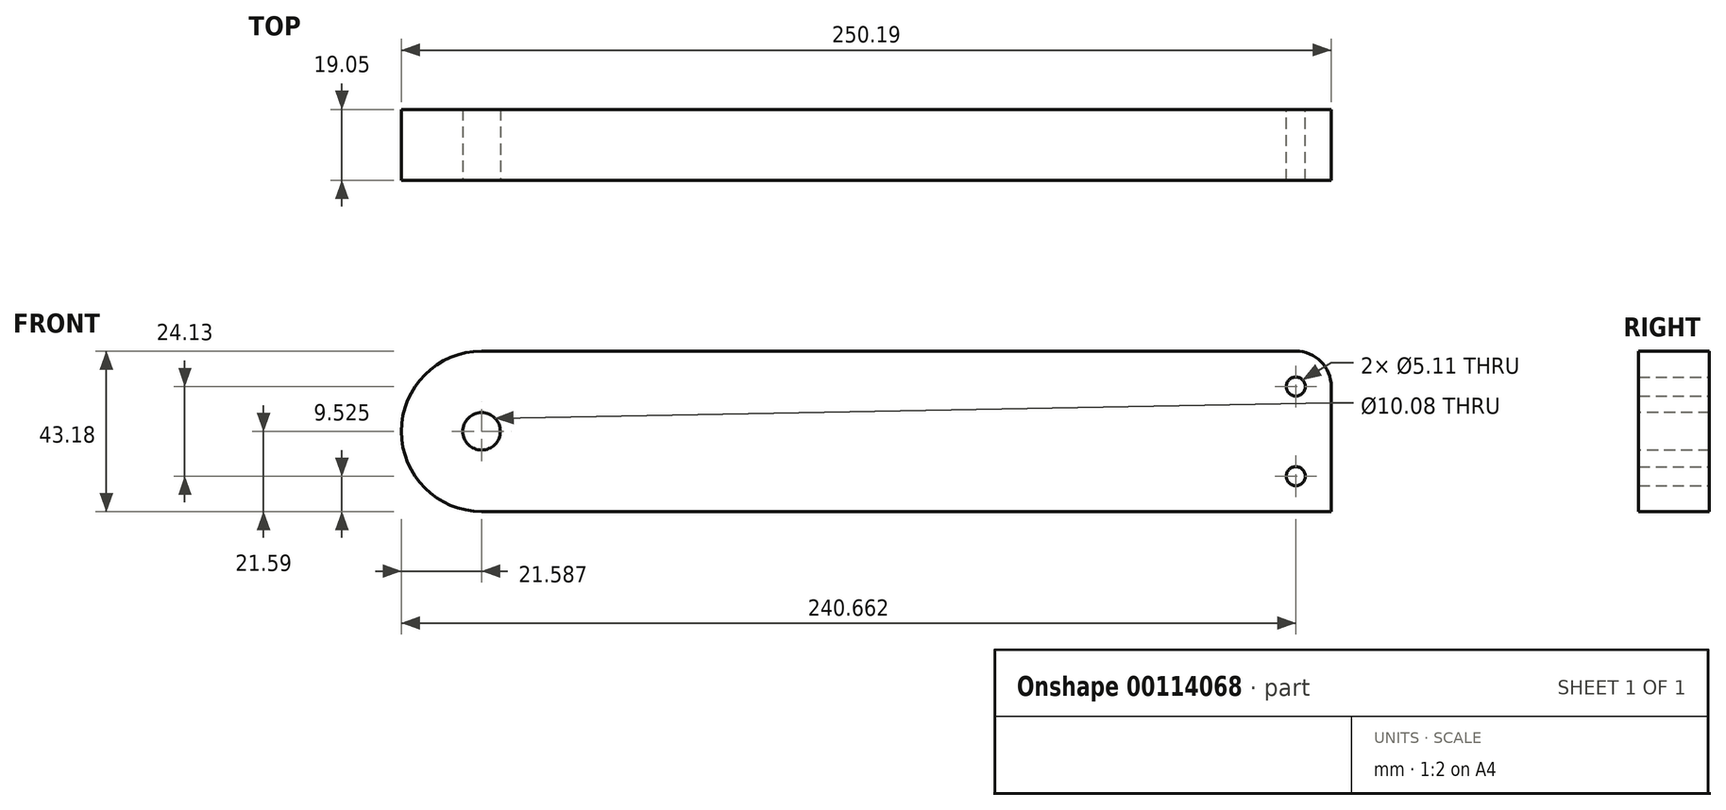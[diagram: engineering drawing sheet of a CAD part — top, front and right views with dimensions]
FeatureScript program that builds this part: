
annotation { "Feature Type Name" : "Feature", "Feature Type Description" : "" }
export const myFeature = defineFeature(function(context is Context, id is Id, definition is map)
    precondition{}
    {
        {
            var Q0;
            Q0=qCreatedBy(makeId("Front.planeOp"),FACE);
            var sketch = newSketch(context, id + "F0", { "sketchPlane" : qUnion([Q0])});
            skLineSegment(sketch, "E0.bottom", {"start": v(-99.87, 43.18) * mm, "end": v(128.73, 43.18) * mm});
            skLineSegment(sketch, "E0.top", {"start": v(-99.87, 0) * mm, "end": v(128.73, 0) * mm});
            skLineSegment(sketch, "E0.right", {"start": v(128.73, 43.18) * mm, "end": v(128.73, 0) * mm});
            skArc(sketch, "E1", {"start": v(-99.87, 0) * mm, "mid": v(-121.46, 21.59) * mm, "end": v(-99.87, 43.18) * mm});
            skSolve(sketch);
        }
        {
            var Q0;
            Q0=qSketchRegion(id+"F0",true);
            extrude(context, id + "F1", {"entities" : qUnion([Q0]), "depth" : 19.05 * mm});
        }
        {
            var Q0;
            Q0=sQuery(id+"F0.wireOp",VERTEX,"E1.center");
            var Q1;
            Q1=makeQuery(id+"F1.opExtrude","SWEPT_BODY",BODY,{"disambiguationData":[OSD([sQuery(id+"F0.wireOp",EDGE,"E0.bottom"),sQuery(id+"F0.wireOp",EDGE,"E0.top"),sQuery(id+"F0.wireOp",EDGE,"E0.right"),sQuery(id+"F0.wireOp",EDGE,"E1")])]});
            hole(context, id + "F2", {"style" : HoleStyle.SIMPLE, "endStyle" : HoleEndStyle.THROUGH, "oppositeDirection" : true, "standardTappedOrClearance" : lookupTablePath({ "standard" : "ANSI", "fit" : "Normal (ASME)", "size" : "3/8", "type" : "Clearance" }), "standardBlindInLast" : lookupTablePath({ "fit" : "Free", "standard" : "ANSI", "size" : "3/8", "type" : "Clearance" }), "holeDiameter" : 10.08 * mm, "locations" : qUnion([Q0]), "scope" : qUnion([Q1]), "isTappedThrough" : true});
        }
        {
            var Q0;
            Q0=makeQuery(id+"F1.opExtrude","SWEPT_EDGE",EDGE,{"disambiguationData":[OSD([sQuery(id+"F0.wireOp",EDGE,"E0.bottom"),sQuery(id+"F0.wireOp",EDGE,"E0.right")])]});
            fillet(context, id + "F3", {"entities" : qUnion([Q0]), "radius" : 9.52 * mm, "tangentPropagation" : true, "allowEdgeOverflow" : false});
        }
        {
            var Q0;
            Q0=makeQuery(id+"F1.opExtrude","CAP_FACE",FACE,{"disambiguationData":[OSD([sQuery(id+"F0.wireOp",EDGE,"E0.bottom"),sQuery(id+"F0.wireOp",EDGE,"E0.top"),sQuery(id+"F0.wireOp",EDGE,"E0.right"),sQuery(id+"F0.wireOp",EDGE,"E1")])],"isStart":false});
            var sketch = newSketch(context, id + "F4", { "sketchPlane" : qUnion([Q0])});
            skLineSegment(sketch, "E2", {"start": v(119.2, 43.18) * mm, "end": v(119.2, 0) * mm, "construction": true});
            skPoint(sketch, "E3", {"position": v(119.2, 33.66) * mm});
            skPoint(sketch, "E4", {"position": v(119.2, 9.53) * mm});
            skSolve(sketch);
        }
        {
            var Q0;
            Q0=sQuery(id+"F4.wireOp",VERTEX,"E3");
            var Q1;
            Q1=sQuery(id+"F4.wireOp",VERTEX,"E4");
            var Q2;
            Q2=makeQuery(id+"F1.opExtrude","SWEPT_BODY",BODY,{"disambiguationData":[OSD([sQuery(id+"F0.wireOp",EDGE,"E0.bottom"),sQuery(id+"F0.wireOp",EDGE,"E0.top"),sQuery(id+"F0.wireOp",EDGE,"E0.right"),sQuery(id+"F0.wireOp",EDGE,"E1")])]});
            hole(context, id + "F5", {"style" : HoleStyle.SIMPLE, "endStyle" : HoleEndStyle.THROUGH, "standardTappedOrClearance" : lookupTablePath({ "standard" : "ANSI", "engagement" : "75%", "pitch" : "20 tpi", "size" : "1/4", "type" : "Tapped" }), "standardBlindInLast" : lookupTablePath({ "standard" : "ANSI", "engagement" : "75%", "pitch" : "20 tpi", "size" : "1/4", "type" : "Tapped" }), "holeDiameter" : 5.1 * mm, "locations" : qUnion([Q0, Q1]), "scope" : qUnion([Q2]), "isTappedThrough" : true, "majorDiameter" : 6.35 * mm, "showTappedDepth" : true});
        }
    });
